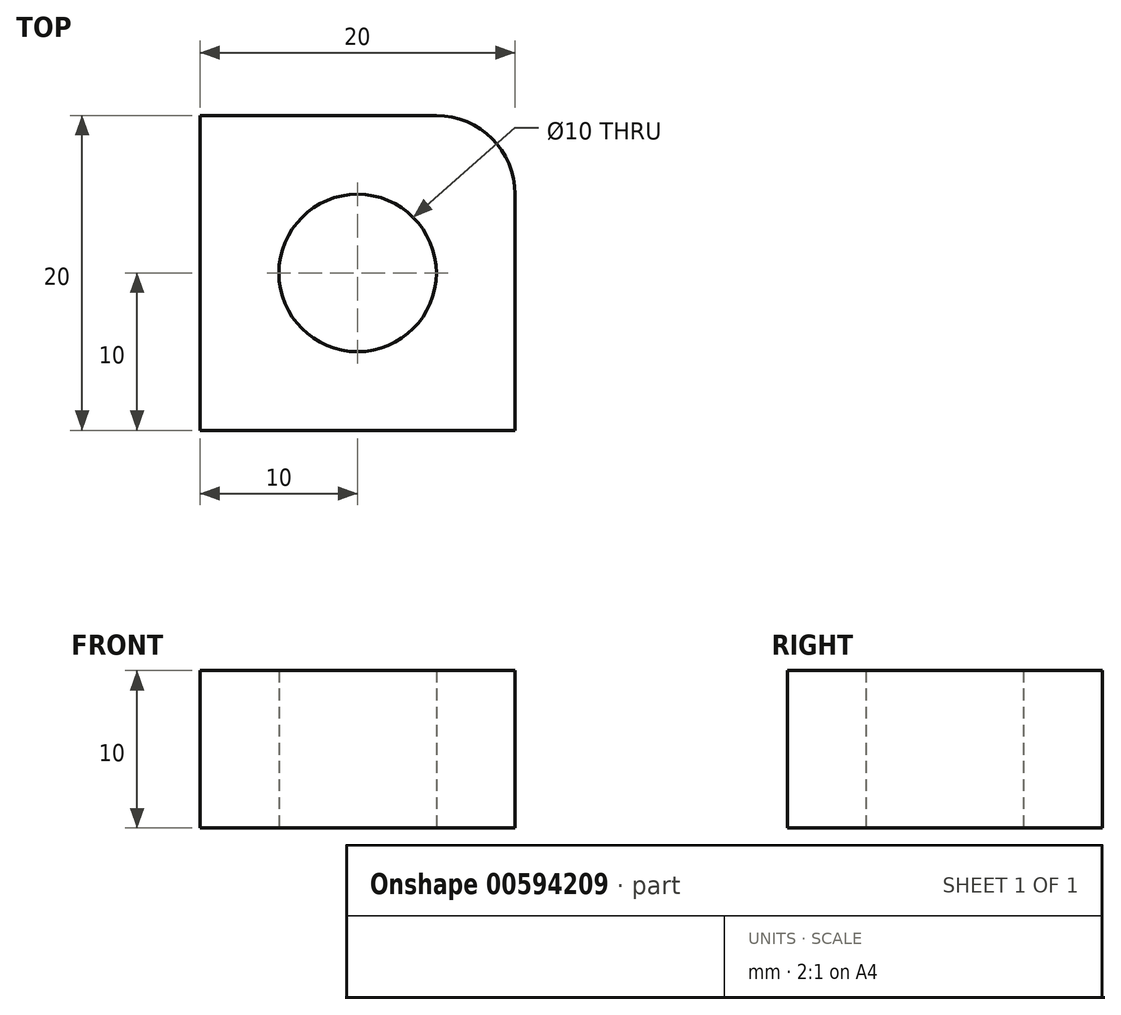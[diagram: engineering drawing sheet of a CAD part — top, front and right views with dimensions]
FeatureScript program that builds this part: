
annotation { "Feature Type Name" : "Feature", "Feature Type Description" : "" }
export const myFeature = defineFeature(function(context is Context, id is Id, definition is map)
    precondition{}
    {
        {
            var Q0;
            Q0=qCreatedBy(makeId("Top.planeOp"),FACE);
            var sketch = newSketch(context, id + "F0", { "sketchPlane" : qUnion([Q0])});
            skLineSegment(sketch, "E0.bottom", {"start": v(10, -10) * mm, "end": v(-10, -10) * mm});
            skLineSegment(sketch, "E0.top", {"start": v(5, 10) * mm, "end": v(-10, 10) * mm});
            skLineSegment(sketch, "E0.left", {"start": v(10, -10) * mm, "end": v(10, 5) * mm});
            skLineSegment(sketch, "E0.right", {"start": v(-10, -10) * mm, "end": v(-10, 10) * mm});
            skPoint(sketch, "E0.middle", {"position": v(0, 0) * mm});
            skCircle(sketch, "E1", {"center": v(0, 0) * mm, "radius": 5 * mm});
            skPoint(sketch, "E2.visualSharp", {"position": v(10, 10) * mm});
            skArc(sketch, "E2.filletArc", {"start": v(10, 5) * mm, "mid": v(8.54, 8.54) * mm, "end": v(5, 10) * mm});
            skSolve(sketch);
        }
        {
            var Q0;
            Q0 = qSketchRegion(id + "F0", true);
            extrude(context, id + "F1", {"entities" : qUnion([Q0]), "depth" : 10 * mm, "offsetDistance" : 25 * mm});
        }
    });
